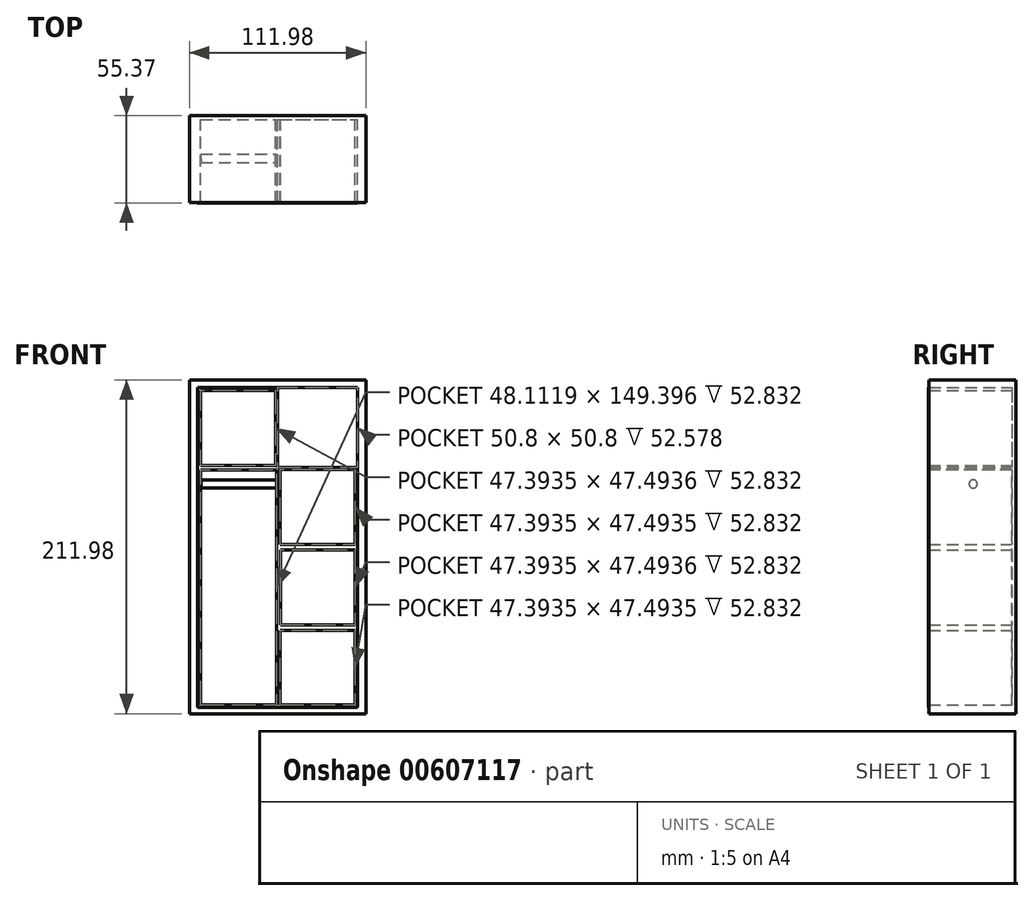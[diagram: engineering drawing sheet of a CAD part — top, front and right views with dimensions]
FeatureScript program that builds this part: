
annotation { "Feature Type Name" : "Feature", "Feature Type Description" : "" }
export const myFeature = defineFeature(function(context is Context, id is Id, definition is map)
    precondition{}
    {
        {
            var Q0;
            Q0=qCreatedBy(makeId("Front.planeOp"),FACE);
            var sketch = newSketch(context, id + "F0", { "sketchPlane" : qUnion([Q0])});
            skLineSegment(sketch, "E0.bottom", {"start": v(-50.04, 148.8) * mm, "end": v(51.56, 148.8) * mm});
            skLineSegment(sketch, "E0.top", {"start": v(-50.04, -54.4) * mm, "end": v(51.56, -54.4) * mm});
            skLineSegment(sketch, "E0.left", {"start": v(-50.04, 148.8) * mm, "end": v(-50.04, -54.4) * mm});
            skLineSegment(sketch, "E0.right", {"start": v(51.56, 148.8) * mm, "end": v(51.56, -54.4) * mm});
            skLineSegment(sketch, "E1.bottom", {"start": v(0.76, 148.8) * mm, "end": v(51.56, 148.8) * mm});
            skLineSegment(sketch, "E1.top", {"start": v(0.76, 98) * mm, "end": v(51.56, 98) * mm});
            skLineSegment(sketch, "E1.left", {"start": v(0.76, 148.8) * mm, "end": v(0.76, 98) * mm});
            skLineSegment(sketch, "E1.right", {"start": v(51.56, 148.8) * mm, "end": v(51.56, 98) * mm});
            skLineSegment(sketch, "E2.top", {"start": v(0.76, 47.2) * mm, "end": v(51.56, 47.2) * mm});
            skLineSegment(sketch, "E2.left", {"start": v(0.76, 98) * mm, "end": v(0.76, 47.2) * mm});
            skLineSegment(sketch, "E2.right", {"start": v(51.56, 98) * mm, "end": v(51.56, 47.2) * mm});
            skLineSegment(sketch, "E3.top", {"start": v(0.76, -3.6) * mm, "end": v(51.56, -3.6) * mm});
            skLineSegment(sketch, "E3.left", {"start": v(0.76, 47.2) * mm, "end": v(0.76, -3.6) * mm});
            skLineSegment(sketch, "E3.right", {"start": v(51.56, 47.2) * mm, "end": v(51.56, -3.6) * mm});
            skLineSegment(sketch, "E4.top", {"start": v(0.76, -54.4) * mm, "end": v(51.56, -54.4) * mm});
            skLineSegment(sketch, "E4.left", {"start": v(0.76, -3.6) * mm, "end": v(0.76, -54.4) * mm});
            skLineSegment(sketch, "E4.right", {"start": v(51.56, -3.6) * mm, "end": v(51.56, -54.4) * mm});
            skLineSegment(sketch, "E5.bottom", {"start": v(0.76, 98) * mm, "end": v(-50.04, 98) * mm});
            skLineSegment(sketch, "E5.top", {"start": v(0.76, 148.8) * mm, "end": v(-50.04, 148.8) * mm});
            skLineSegment(sketch, "E5.left", {"start": v(0.76, 98) * mm, "end": v(0.76, 148.8) * mm});
            skLineSegment(sketch, "E5.right", {"start": v(-50.04, 98) * mm, "end": v(-50.04, 148.8) * mm});
            skLineSegment(sketch, "E6.bottom", {"start": v(-55.14, 153.62) * mm, "end": v(56.84, 153.62) * mm});
            skLineSegment(sketch, "E6.top", {"start": v(-55.14, -58.36) * mm, "end": v(56.84, -58.36) * mm});
            skLineSegment(sketch, "E6.left", {"start": v(-55.14, 153.62) * mm, "end": v(-55.14, -58.36) * mm});
            skLineSegment(sketch, "E6.right", {"start": v(56.84, 153.62) * mm, "end": v(56.84, -58.36) * mm});
            skLineSegment(sketch, "E7.bottom", {"start": v(-48.11, 146.85) * mm, "end": v(-0.72, 146.85) * mm});
            skLineSegment(sketch, "E7.top", {"start": v(-48.11, 99.36) * mm, "end": v(-0.72, 99.36) * mm});
            skLineSegment(sketch, "E7.left", {"start": v(-48.11, 146.85) * mm, "end": v(-48.11, 99.36) * mm});
            skLineSegment(sketch, "E7.right", {"start": v(-0.72, 146.85) * mm, "end": v(-0.72, 99.36) * mm});
            skLineSegment(sketch, "E8.bottom", {"start": v(2.62, 146.95) * mm, "end": v(50, 146.95) * mm});
            skLineSegment(sketch, "E8.top", {"start": v(2.62, 99.46) * mm, "end": v(50, 99.46) * mm});
            skLineSegment(sketch, "E8.left", {"start": v(2.62, 146.95) * mm, "end": v(2.62, 99.46) * mm});
            skLineSegment(sketch, "E8.right", {"start": v(50, 146.95) * mm, "end": v(50, 99.46) * mm});
            skLineSegment(sketch, "E9.bottom", {"start": v(2.45, 96.72) * mm, "end": v(49.85, 96.72) * mm});
            skLineSegment(sketch, "E9.top", {"start": v(2.45, 49.23) * mm, "end": v(49.85, 49.23) * mm});
            skLineSegment(sketch, "E9.left", {"start": v(2.45, 96.72) * mm, "end": v(2.45, 49.23) * mm});
            skLineSegment(sketch, "E9.right", {"start": v(49.85, 96.72) * mm, "end": v(49.85, 49.23) * mm});
            skLineSegment(sketch, "E10.bottom", {"start": v(2.57, 45.66) * mm, "end": v(49.96, 45.66) * mm});
            skLineSegment(sketch, "E10.top", {"start": v(2.57, -1.83) * mm, "end": v(49.96, -1.83) * mm});
            skLineSegment(sketch, "E10.left", {"start": v(2.57, 45.66) * mm, "end": v(2.57, -1.83) * mm});
            skLineSegment(sketch, "E10.right", {"start": v(49.96, 45.66) * mm, "end": v(49.96, -1.83) * mm});
            skLineSegment(sketch, "E11.bottom", {"start": v(2.38, -5.36) * mm, "end": v(49.77, -5.36) * mm});
            skLineSegment(sketch, "E11.top", {"start": v(2.38, -52.86) * mm, "end": v(49.77, -52.86) * mm});
            skLineSegment(sketch, "E11.left", {"start": v(2.38, -5.36) * mm, "end": v(2.38, -52.86) * mm});
            skLineSegment(sketch, "E11.right", {"start": v(49.77, -5.36) * mm, "end": v(49.77, -52.86) * mm});
            skSolve(sketch);
        }
        {
            var Q0;
            Q0 = qSketchRegion(id + "F0", true);
            extrude(context, id + "F1", {"entities" : qUnion([Q0]), "depth" : 52.58 * mm, "offsetDistance" : 25.4 * mm});
        }
        {
            var Q0;
            Q0=makeQuery(id+"F0.imprint","IMPRINT",FACE,{"disambiguationData":[TD([[makeQuery(id+"F0.imprint","IMPRINT",EDGE,{"derivedFrom":sQuery(id+"F0.wireOp",EDGE,"E5.bottom")}),-1.0]])]});
            var Q1;
            Q1=makeQuery(id+"F0.imprint","IMPRINT",FACE,{"disambiguationData":[TD([[makeQuery(id+"F0.imprint","IMPRINT",EDGE,{"derivedFrom":sQuery(id+"F0.wireOp",EDGE,"E1.bottom")}),-1.0]])]});
            var Q2;
            Q2=makeQuery(id+"F0.imprint","IMPRINT",FACE,{"disambiguationData":[TD([[makeQuery(id+"F0.imprint","IMPRINT",EDGE,{"derivedFrom":sQuery(id+"F0.wireOp",EDGE,"E1.top")}),-1.0]])]});
            var Q3;
            Q3=makeQuery(id+"F0.imprint","IMPRINT",FACE,{"disambiguationData":[TD([[makeQuery(id+"F0.imprint","IMPRINT",EDGE,{"derivedFrom":sQuery(id+"F0.wireOp",EDGE,"E0.top")}),1.0]])]});
            var Q4;
            Q4=makeQuery(id+"F0.imprint","IMPRINT",FACE,{"disambiguationData":[TD([[makeQuery(id+"F0.imprint","IMPRINT",EDGE,{"derivedFrom":sQuery(id+"F0.wireOp",EDGE,"E2.top")}),-1.0]])]});
            var Q5;
            Q5=makeQuery(id+"F0.imprint","IMPRINT",FACE,{"disambiguationData":[TD([[makeQuery(id+"F0.imprint","IMPRINT",EDGE,{"derivedFrom":sQuery(id+"F0.wireOp",EDGE,"E3.top")}),-1.0]])]});
            extrude(context, id + "F2", {"entities" : qUnion([Q0, Q1, Q2, Q3, Q4, Q5]), "operationType" : NewBodyOperationType.ADD, "depth" : 52.83 * mm, "offsetDistance" : 25.4 * mm});
        }
        {
            var Q0;
            Q0=makeQuery(id+"F2.opExtrude","CAP_FACE",FACE,{"disambiguationData":[OSD([sQuery(id+"F0.wireOp",EDGE,"E0.top"),sQuery(id+"F0.wireOp",EDGE,"E0.left"),sQuery(id+"F0.wireOp",EDGE,"E1.bottom"),sQuery(id+"F0.wireOp",EDGE,"E1.right"),sQuery(id+"F0.wireOp",EDGE,"E2.right"),sQuery(id+"F0.wireOp",EDGE,"E3.right"),sQuery(id+"F0.wireOp",EDGE,"E4.top"),sQuery(id+"F0.wireOp",EDGE,"E4.right"),sQuery(id+"F0.wireOp",EDGE,"E5.top"),sQuery(id+"F0.wireOp",EDGE,"E5.right"),sQuery(id+"F0.wireOp",EDGE,"E7.bottom"),sQuery(id+"F0.wireOp",EDGE,"E7.top"),sQuery(id+"F0.wireOp",EDGE,"E7.left"),sQuery(id+"F0.wireOp",EDGE,"E7.right"),sQuery(id+"F0.wireOp",EDGE,"E8.bottom"),sQuery(id+"F0.wireOp",EDGE,"E8.top"),sQuery(id+"F0.wireOp",EDGE,"E8.left"),sQuery(id+"F0.wireOp",EDGE,"E8.right"),sQuery(id+"F0.wireOp",EDGE,"E9.bottom"),sQuery(id+"F0.wireOp",EDGE,"E9.top"),sQuery(id+"F0.wireOp",EDGE,"E9.left"),sQuery(id+"F0.wireOp",EDGE,"E9.right"),sQuery(id+"F0.wireOp",EDGE,"E10.bottom"),sQuery(id+"F0.wireOp",EDGE,"E10.top"),sQuery(id+"F0.wireOp",EDGE,"E10.left"),sQuery(id+"F0.wireOp",EDGE,"E10.right"),sQuery(id+"F0.wireOp",EDGE,"E11.bottom"),sQuery(id+"F0.wireOp",EDGE,"E11.top"),sQuery(id+"F0.wireOp",EDGE,"E11.left"),sQuery(id+"F0.wireOp",EDGE,"E11.right")])],"isStart":false});
            var sketch = newSketch(context, id + "F3", { "sketchPlane" : qUnion([Q0])});
            skLineSegment(sketch, "E12.bottom", {"start": v(-48.11, -52.86) * mm, "end": v(0, -52.86) * mm});
            skLineSegment(sketch, "E12.top", {"start": v(-48.11, 96.54) * mm, "end": v(0, 96.54) * mm});
            skLineSegment(sketch, "E12.left", {"start": v(-48.11, -52.86) * mm, "end": v(-48.11, 96.54) * mm});
            skLineSegment(sketch, "E12.right", {"start": v(0, -52.86) * mm, "end": v(0, 96.54) * mm});
            skSolve(sketch);
        }
        {
            var Q0;
            Q0=makeQuery(id+"F3.imprint","IMPRINT",FACE,{"disambiguationData":[TD([[makeQuery(id+"F3.imprint","IMPRINT",EDGE,{"derivedFrom":sQuery(id+"F3.wireOp",EDGE,"E12.bottom")}),1.0]])]});
            extrude(context, id + "F4", {"entities" : qUnion([Q0]), "operationType" : NewBodyOperationType.REMOVE, "oppositeDirection" : true, "depth" : 53.6 * mm, "offsetDistance" : 25.4 * mm});
        }
        {
            var Q0;
            {var subQ0=sQuery(id+"F0.wireOp",EDGE,"E5.right");var subQ1=sQuery(id+"F0.wireOp",EDGE,"E5.top");var subQ2=sQuery(id+"F0.wireOp",EDGE,"E4.right");var subQ3=sQuery(id+"F0.wireOp",EDGE,"E4.top");var subQ4=sQuery(id+"F0.wireOp",EDGE,"E3.right");var subQ5=sQuery(id+"F0.wireOp",EDGE,"E2.right");var subQ6=sQuery(id+"F0.wireOp",EDGE,"E1.right");var subQ7=sQuery(id+"F0.wireOp",EDGE,"E1.bottom");var subQ8=sQuery(id+"F0.wireOp",EDGE,"E0.left");var subQ9=sQuery(id+"F0.wireOp",EDGE,"E0.top");Q0=makeQuery(id+"F2.boolean.opBoolean","MERGE",FACE,{"derivedFrom":[makeQuery(id+"F1.opExtrude","CAP_FACE",FACE,{"disambiguationData":[OSD([subQ9,subQ8,subQ7,subQ6,subQ5,subQ4,subQ3,subQ2,subQ1,subQ0,sQuery(id+"F0.wireOp",EDGE,"E6.bottom"),sQuery(id+"F0.wireOp",EDGE,"E6.top"),sQuery(id+"F0.wireOp",EDGE,"E6.left"),sQuery(id+"F0.wireOp",EDGE,"E6.right")])],"isStart":true}),makeQuery(id+"F2.opExtrude","CAP_FACE",FACE,{"disambiguationData":[OSD([subQ9,subQ8,subQ7,subQ6,subQ5,subQ4,subQ3,subQ2,subQ1,subQ0,sQuery(id+"F0.wireOp",EDGE,"E7.bottom"),sQuery(id+"F0.wireOp",EDGE,"E7.top"),sQuery(id+"F0.wireOp",EDGE,"E7.left"),sQuery(id+"F0.wireOp",EDGE,"E7.right"),sQuery(id+"F0.wireOp",EDGE,"E8.bottom"),sQuery(id+"F0.wireOp",EDGE,"E8.top"),sQuery(id+"F0.wireOp",EDGE,"E8.left"),sQuery(id+"F0.wireOp",EDGE,"E8.right"),sQuery(id+"F0.wireOp",EDGE,"E9.bottom"),sQuery(id+"F0.wireOp",EDGE,"E9.top"),sQuery(id+"F0.wireOp",EDGE,"E9.left"),sQuery(id+"F0.wireOp",EDGE,"E9.right"),sQuery(id+"F0.wireOp",EDGE,"E10.bottom"),sQuery(id+"F0.wireOp",EDGE,"E10.top"),sQuery(id+"F0.wireOp",EDGE,"E10.left"),sQuery(id+"F0.wireOp",EDGE,"E10.right"),sQuery(id+"F0.wireOp",EDGE,"E11.bottom"),sQuery(id+"F0.wireOp",EDGE,"E11.top"),sQuery(id+"F0.wireOp",EDGE,"E11.left"),sQuery(id+"F0.wireOp",EDGE,"E11.right")])],"isStart":true})]});}
            var sketch = newSketch(context, id + "F5", { "sketchPlane" : qUnion([Q0])});
            skLineSegment(sketch, "E13.bottom", {"start": v(-56.84, 153.62) * mm, "end": v(55.14, 153.62) * mm});
            skLineSegment(sketch, "E13.top", {"start": v(-56.84, -58.36) * mm, "end": v(55.14, -58.36) * mm});
            skLineSegment(sketch, "E13.left", {"start": v(-56.84, 153.62) * mm, "end": v(-56.84, -58.36) * mm});
            skLineSegment(sketch, "E13.right", {"start": v(55.14, 153.62) * mm, "end": v(55.14, -58.36) * mm});
            skSolve(sketch);
        }
        {
            var Q0;
            Q0 = qSketchRegion(id + "F5", true);
            extrude(context, id + "F6", {"entities" : qUnion([Q0]), "operationType" : NewBodyOperationType.ADD, "depth" : 2.54 * mm, "offsetDistance" : 25.4 * mm});
        }
        {
            var Q0;
            Q0=makeQuery(id+"F4.boolean.opBoolean","COPY",FACE,{"derivedFrom":makeQuery(id+"F4.opExtrude","SWEPT_FACE",FACE,{"disambiguationData":[OSD([sQuery(id+"F3.wireOp",EDGE,"E12.right")])]})});
            var sketch = newSketch(context, id + "F7", { "sketchPlane" : qUnion([Q0])});
            skCircle(sketch, "E14", {"center": v(24.55, 87.59) * mm, "radius": 2.65 * mm});
            skSolve(sketch);
        }
        {
            var Q0;
            Q0 = qSketchRegion(id + "F7", true);
            extrude(context, id + "F8", {"entities" : qUnion([Q0]), "operationType" : NewBodyOperationType.ADD, "depth" : 48 * mm, "offsetDistance" : 25.4 * mm});
        }
    });
